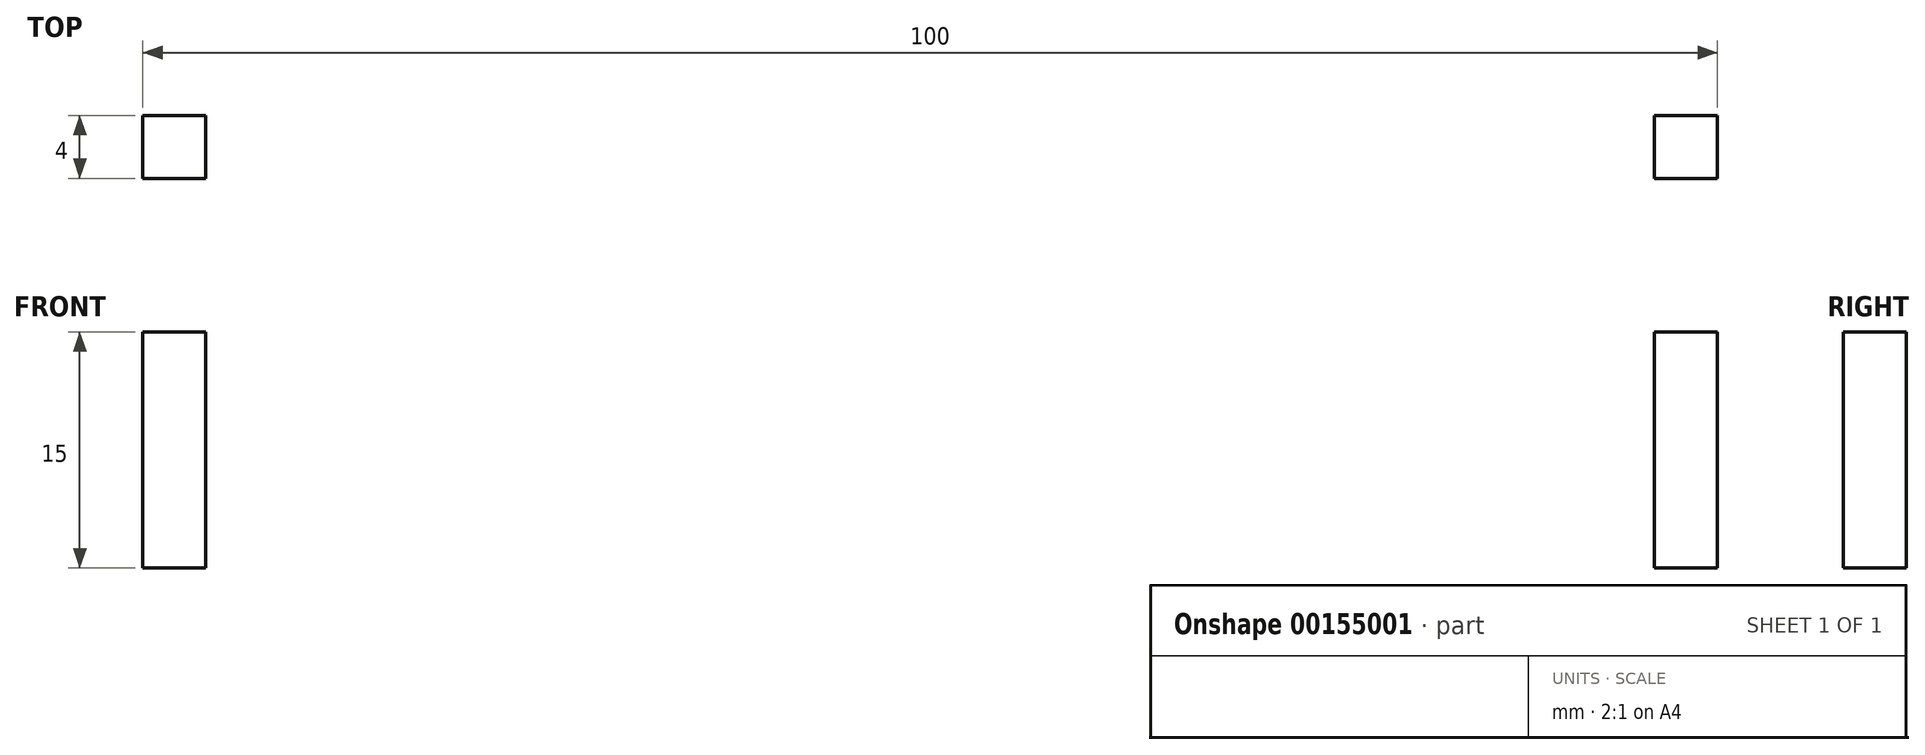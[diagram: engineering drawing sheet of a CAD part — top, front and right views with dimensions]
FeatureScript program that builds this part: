
annotation { "Feature Type Name" : "Feature", "Feature Type Description" : "" }
export const myFeature = defineFeature(function(context is Context, id is Id, definition is map)
    precondition{}
    {
        {
            var Q0;
            Q0=qCreatedBy(makeId("Front.planeOp"),FACE);
            var sketch = newSketch(context, id + "F0", { "sketchPlane" : qUnion([Q0])});
            skLineSegment(sketch, "E0.bottom", {"start": v(0, 50) * mm, "end": v(100, 50) * mm});
            skLineSegment(sketch, "E0.top", {"start": v(0, 0) * mm, "end": v(100, 0) * mm});
            skLineSegment(sketch, "E0.left", {"start": v(0, 50) * mm, "end": v(0, 0) * mm});
            skLineSegment(sketch, "E0.right", {"start": v(100, 50) * mm, "end": v(100, 0) * mm});
            skLineSegment(sketch, "E1.top", {"start": v(20, 0) * mm, "end": v(40, 0) * mm});
            skLineSegment(sketch, "E1.left", {"start": v(20, 4) * mm, "end": v(20, 0) * mm});
            skLineSegment(sketch, "E1.right", {"start": v(40, 4) * mm, "end": v(40, 0) * mm});
            skLineSegment(sketch, "E2.top", {"start": v(60, 0) * mm, "end": v(80, 0) * mm});
            skLineSegment(sketch, "E2.left", {"start": v(60, 4) * mm, "end": v(60, 0) * mm});
            skLineSegment(sketch, "E2.right", {"start": v(80, 4) * mm, "end": v(80, 0) * mm});
            skLineSegment(sketch, "E3.bottom", {"start": v(96, 35) * mm, "end": v(100, 35) * mm});
            skLineSegment(sketch, "E3.top", {"start": v(96, 15) * mm, "end": v(100, 15) * mm});
            skLineSegment(sketch, "E3.right", {"start": v(100, 35) * mm, "end": v(100, 15) * mm});
            skPoint(sketch, "E4.oppositeSnap0", {"position": v(0, 25) * mm});
            skLineSegment(sketch, "E4.bottom", {"start": v(4, 35) * mm, "end": v(0, 35) * mm});
            skLineSegment(sketch, "E4.top", {"start": v(4, 15) * mm, "end": v(0, 15) * mm});
            skLineSegment(sketch, "E4.right", {"start": v(0, 35) * mm, "end": v(0, 15) * mm});
            skLineSegment(sketch, "E5.top", {"start": v(4, 0) * mm, "end": v(0, 0) * mm});
            skLineSegment(sketch, "E5.left", {"start": v(4, 15) * mm, "end": v(4, 0) * mm});
            skLineSegment(sketch, "E5.right", {"start": v(0, 15) * mm, "end": v(0, 0) * mm});
            skLineSegment(sketch, "E6.top", {"start": v(4, 50) * mm, "end": v(0, 50) * mm});
            skLineSegment(sketch, "E6.left", {"start": v(4, 35) * mm, "end": v(4, 50) * mm});
            skLineSegment(sketch, "E6.right", {"start": v(0, 35) * mm, "end": v(0, 50) * mm});
            skLineSegment(sketch, "E7.top", {"start": v(96, 50) * mm, "end": v(100, 50) * mm});
            skLineSegment(sketch, "E7.left", {"start": v(96, 35) * mm, "end": v(96, 50) * mm});
            skLineSegment(sketch, "E7.right", {"start": v(100, 35) * mm, "end": v(100, 50) * mm});
            skLineSegment(sketch, "E8.top", {"start": v(96, 0) * mm, "end": v(100, 0) * mm});
            skLineSegment(sketch, "E8.left", {"start": v(96, 15) * mm, "end": v(96, 0) * mm});
            skLineSegment(sketch, "E8.right", {"start": v(100, 15) * mm, "end": v(100, 0) * mm});
            skLineSegment(sketch, "E9.bottom", {"start": v(20, 4) * mm, "end": v(4, 4) * mm});
            skLineSegment(sketch, "E9.top", {"start": v(20, 0) * mm, "end": v(4, 0) * mm});
            skLineSegment(sketch, "E9.right", {"start": v(4, 4) * mm, "end": v(4, 0) * mm});
            skLineSegment(sketch, "E10.bottom", {"start": v(40, 4) * mm, "end": v(60, 4) * mm});
            skLineSegment(sketch, "E10.top", {"start": v(40, 0) * mm, "end": v(60, 0) * mm});
            skLineSegment(sketch, "E11.bottom", {"start": v(80, 4) * mm, "end": v(96, 4) * mm});
            skLineSegment(sketch, "E11.top", {"start": v(80, 0) * mm, "end": v(96, 0) * mm});
            skLineSegment(sketch, "E11.right", {"start": v(96, 4) * mm, "end": v(96, 0) * mm});
            skSolve(sketch);
        }
        {
            var Q0;
            {var subQ5=sQuery(id+"F0.wireOp",EDGE,"E0.bottom");Q0=makeQuery(id+"F0.imprint","IMPRINT",FACE,{"disambiguationData":[TD([[makeQuery(id+"F0.imprint","IMPRINT",EDGE,{"derivedFrom":subQ5}),-1.0]])]});}
            extrude(context, id + "F1", {"entities" : qUnion([Q0]), "depth" : 4 * mm});
        }
    });
